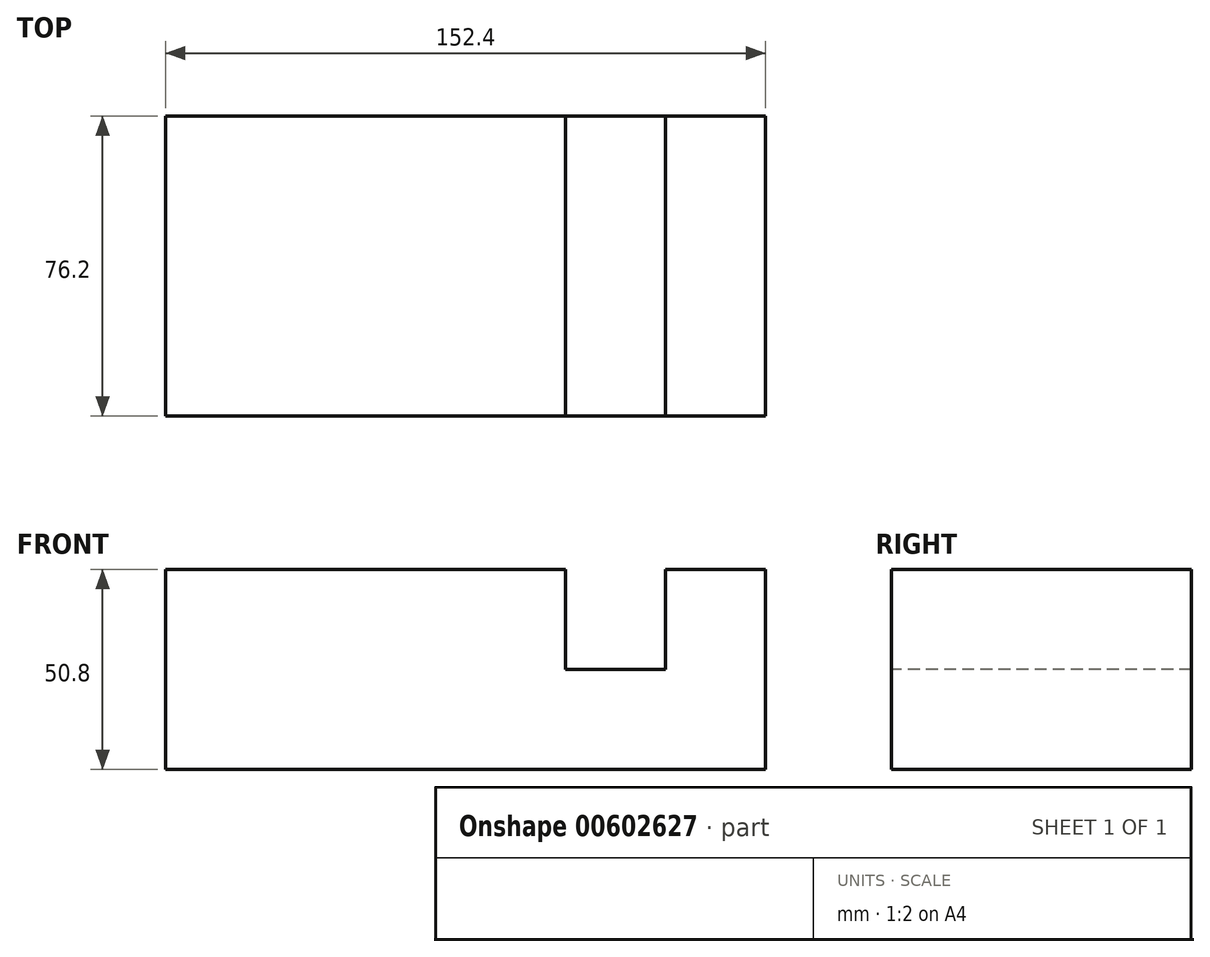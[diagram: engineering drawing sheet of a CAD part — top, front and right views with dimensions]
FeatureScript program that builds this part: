
annotation { "Feature Type Name" : "Feature", "Feature Type Description" : "" }
export const myFeature = defineFeature(function(context is Context, id is Id, definition is map)
    precondition{}
    {
        {
            var Q0;
            Q0=qCreatedBy(makeId("Front.planeOp"),FACE);
            var sketch = newSketch(context, id + "F0", { "sketchPlane" : qUnion([Q0])});
            skLineSegment(sketch, "E0", {"start": v(0, 0) * mm, "end": v(152.4, 0) * mm});
            skLineSegment(sketch, "E1", {"start": v(152.4, 0) * mm, "end": v(152.4, 50.8) * mm});
            skLineSegment(sketch, "E2", {"start": v(152.4, 50.8) * mm, "end": v(127, 50.8) * mm});
            skLineSegment(sketch, "E3", {"start": v(127, 50.8) * mm, "end": v(127, 25.4) * mm});
            skLineSegment(sketch, "E4", {"start": v(127, 25.4) * mm, "end": v(101.6, 25.4) * mm});
            skLineSegment(sketch, "E5", {"start": v(101.6, 25.4) * mm, "end": v(101.6, 50.8) * mm});
            skLineSegment(sketch, "E6", {"start": v(101.6, 50.8) * mm, "end": v(0, 50.8) * mm});
            skLineSegment(sketch, "E7", {"start": v(0, 50.8) * mm, "end": v(0, 0) * mm});
            skSolve(sketch);
        }
        {
            var Q0;
            Q0 = qSketchRegion(id + "F0", true);
            extrude(context, id + "F1", {"entities" : qUnion([Q0]), "oppositeDirection" : true, "depth" : 76.2 * mm, "offsetDistance" : 25.4 * mm});
        }
    });
